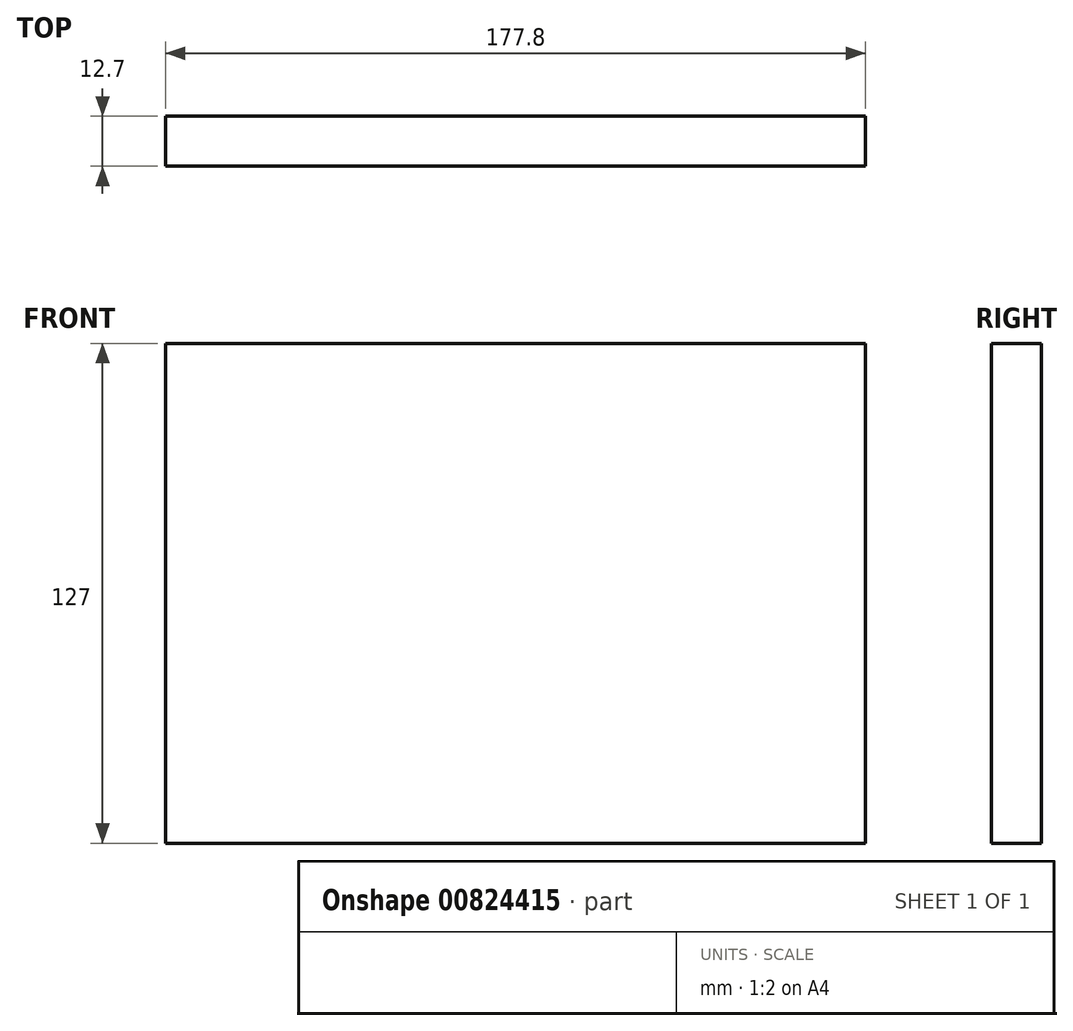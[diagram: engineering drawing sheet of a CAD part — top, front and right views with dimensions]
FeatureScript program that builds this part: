
annotation { "Feature Type Name" : "Feature", "Feature Type Description" : "" }
export const myFeature = defineFeature(function(context is Context, id is Id, definition is map)
    precondition{}
    {
        {
            var Q0;
            Q0=qCreatedBy(makeId("Front.planeOp"),FACE);
            var sketch = newSketch(context, id + "F0", { "sketchPlane" : qUnion([Q0])});
            skLineSegment(sketch, "E0", {"start": v(-87.23, 35) * mm, "end": v(-87.23, -92) * mm});
            skLineSegment(sketch, "E1", {"start": v(-87.23, -92) * mm, "end": v(90.57, -92) * mm});
            skLineSegment(sketch, "E2", {"start": v(90.57, -92) * mm, "end": v(90.57, 35) * mm});
            skLineSegment(sketch, "E3", {"start": v(-87.23, 35) * mm, "end": v(90.57, 35) * mm});
            skSolve(sketch);
        }
        {
            var Q0;
            Q0 = qSketchRegion(id + "F0", true);
            extrude(context, id + "F1", {"entities" : qUnion([Q0]), "depth" : 12.7 * mm, "offsetDistance" : 25.4 * mm});
        }
    });
